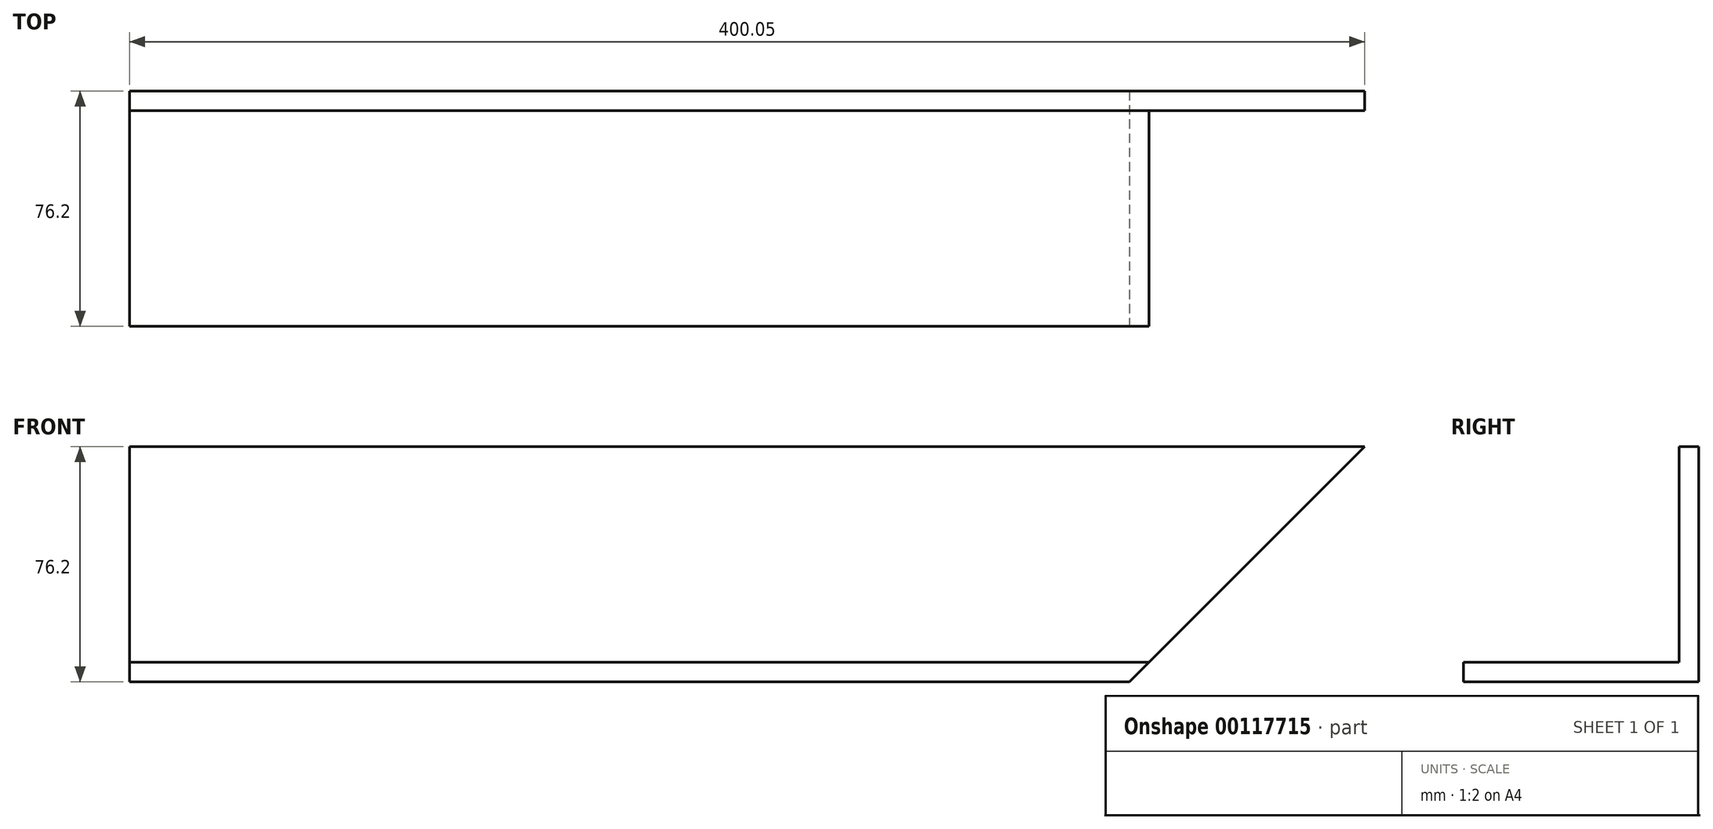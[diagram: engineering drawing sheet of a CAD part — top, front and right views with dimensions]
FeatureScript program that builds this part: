
annotation { "Feature Type Name" : "Feature", "Feature Type Description" : "" }
export const myFeature = defineFeature(function(context is Context, id is Id, definition is map)
    precondition{}
    {
        {
            var Q0;
            Q0=qCreatedBy(makeId("Front.planeOp"),FACE);
            var sketch = newSketch(context, id + "F0", { "sketchPlane" : qUnion([Q0])});
            skLineSegment(sketch, "E0", {"start": v(-278.97, 7.36) * mm, "end": v(51.23, 7.36) * mm});
            skLineSegment(sketch, "E1", {"start": v(121.08, 77.21) * mm, "end": v(-278.97, 77.21) * mm});
            skLineSegment(sketch, "E2", {"start": v(-278.97, 7.36) * mm, "end": v(-278.97, 77.21) * mm});
            skLineSegment(sketch, "E3", {"start": v(51.23, 7.36) * mm, "end": v(121.08, 77.21) * mm});
            skPoint(sketch, "E4.start.orphan", {"position": v(-348.82, 77.21) * mm});
            skLineSegment(sketch, "E5.top", {"start": v(-278.97, 1.01) * mm, "end": v(51.23, 1.01) * mm});
            skLineSegment(sketch, "E5.left", {"start": v(-278.97, 7.36) * mm, "end": v(-278.97, 1.01) * mm});
            skLineSegment(sketch, "E5.right", {"start": v(51.23, 7.36) * mm, "end": v(51.23, 1.01) * mm});
            skSolve(sketch);
        }
        {
            var Q0;
            Q0=makeQuery(id+"F0.imprint","IMPRINT",FACE,{"disambiguationData":[TD([[makeQuery(id+"F0.imprint","IMPRINT",EDGE,{"derivedFrom":sQuery(id+"F0.wireOp",EDGE,"E1")}),1.0]])]});
            extrude(context, id + "F1", {"entities" : qUnion([Q0]), "depth" : 6.35 * mm});
        }
        {
            var Q0;
            Q0=makeQuery(id+"F0.imprint","IMPRINT",FACE,{"disambiguationData":[TD([[makeQuery(id+"F0.imprint","IMPRINT",EDGE,{"derivedFrom":sQuery(id+"F0.wireOp",EDGE,"E0")}),-1.0]])]});
            extrude(context, id + "F2", {"entities" : qUnion([Q0]), "operationType" : NewBodyOperationType.ADD, "depth" : 76.2 * mm});
        }
        {
            var Q0;
            Q0=makeQuery(id+"F2.opExtrude","SWEPT_EDGE",EDGE,{"disambiguationData":[OSD([sQuery(id+"F0.wireOp",EDGE,"E5.top"),sQuery(id+"F0.wireOp",EDGE,"E5.right")])]});
            chamfer(context, id + "F3", {"entities" : qUnion([Q0]), "width" : 6.35 * mm, "tangentPropagation" : true});
        }
    });
